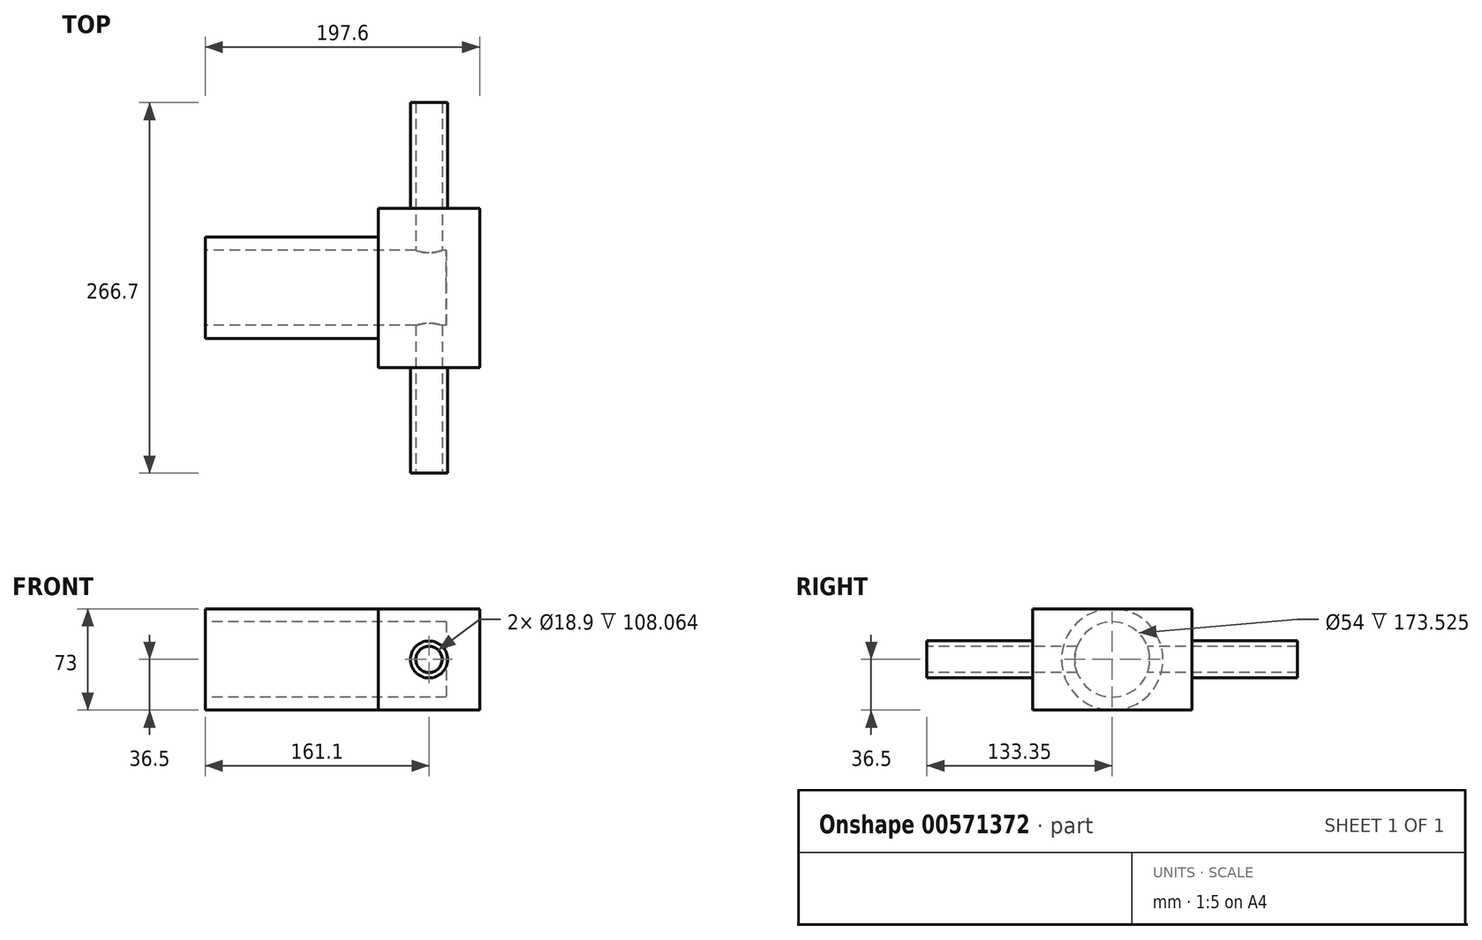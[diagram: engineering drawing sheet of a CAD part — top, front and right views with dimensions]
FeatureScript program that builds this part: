
annotation { "Feature Type Name" : "Feature", "Feature Type Description" : "" }
export const myFeature = defineFeature(function(context is Context, id is Id, definition is map)
    precondition{}
    {
        {
            var Q0;
            Q0=qCreatedBy(makeId("Front.planeOp"),FACE);
            var sketch = newSketch(context, id + "F0", { "sketchPlane" : qUnion([Q0])});
            skLineSegment(sketch, "E0.bottom", {"start": v(-36.5, -36.5) * mm, "end": v(36.5, -36.5) * mm});
            skLineSegment(sketch, "E0.top", {"start": v(-36.5, 36.5) * mm, "end": v(36.5, 36.5) * mm});
            skLineSegment(sketch, "E0.left", {"start": v(-36.5, -36.5) * mm, "end": v(-36.5, 36.5) * mm});
            skLineSegment(sketch, "E0.right", {"start": v(36.5, -36.5) * mm, "end": v(36.5, 36.5) * mm});
            skPoint(sketch, "E0.middle", {"position": v(0, 0) * mm});
            skSolve(sketch);
        }
        {
            var Q0;
            Q0 = qSketchRegion(id + "F0", true);
            extrude(context, id + "F1", {"entities" : qUnion([Q0]), "endBound" : BoundingType.SYMMETRIC, "depth" : 266.7 * mm, "offsetDistance" : 25 * mm});
        }
        {
            var Q0;
            Q0=qCreatedBy(makeId("Right.planeOp"),FACE);
            var sketch = newSketch(context, id + "F2", { "sketchPlane" : qUnion([Q0])});
            skCircle(sketch, "E1", {"center": v(0, 0) * mm, "radius": 36.5 * mm});
            skSolve(sketch);
        }
        {
            var Q0;
            Q0 = qSketchRegion(id + "F2", true);
            extrude(context, id + "F3", {"entities" : qUnion([Q0]), "operationType" : NewBodyOperationType.ADD, "oppositeDirection" : true, "depth" : 161.1 * mm, "offsetDistance" : 25 * mm});
        }
        {
            var Q0;
            Q0=makeQuery(id+"F3.opExtrude","CAP_FACE",FACE,{"disambiguationData":[OSD([sQuery(id+"F2.wireOp",EDGE,"E1")])],"isStart":false});
            var sketch = newSketch(context, id + "F4", { "sketchPlane" : qUnion([Q0])});
            skCircle(sketch, "E2", {"center": v(0, 0) * mm, "radius": 27 * mm});
            skSolve(sketch);
        }
        {
            var Q0;
            Q0 = qSketchRegion(id + "F4", true);
            extrude(context, id + "F5", {"entities" : qUnion([Q0]), "operationType" : NewBodyOperationType.REMOVE, "oppositeDirection" : true, "depth" : (12.43 + 161.1) * mm, "offsetDistance" : 25 * mm});
        }
        {
            var Q0;
            Q0=makeQuery(id+"F1.opExtrude","CAP_FACE",FACE,{"disambiguationData":[OSD([sQuery(id+"F0.wireOp",EDGE,"E0.bottom"),sQuery(id+"F0.wireOp",EDGE,"E0.top"),sQuery(id+"F0.wireOp",EDGE,"E0.left"),sQuery(id+"F0.wireOp",EDGE,"E0.right")])],"isStart":false});
            var sketch = newSketch(context, id + "F6", { "sketchPlane" : qUnion([Q0])});
            skCircle(sketch, "E3", {"center": v(0, 0) * mm, "radius": 9.45 * mm});
            skSolve(sketch);
        }
        {
            var Q0;
            Q0 = qSketchRegion(id + "F6", true);
            extrude(context, id + "F7", {"entities" : qUnion([Q0]), "operationType" : NewBodyOperationType.REMOVE, "oppositeDirection" : true, "depth" : 336 * mm, "offsetDistance" : 25 * mm});
        }
        {
            var Q0;
            Q0=makeQuery(id+"F1.opExtrude","CAP_FACE",FACE,{"disambiguationData":[OSD([sQuery(id+"F0.wireOp",EDGE,"E0.bottom"),sQuery(id+"F0.wireOp",EDGE,"E0.top"),sQuery(id+"F0.wireOp",EDGE,"E0.left"),sQuery(id+"F0.wireOp",EDGE,"E0.right")])],"isStart":true});
            var sketch = newSketch(context, id + "F8", { "sketchPlane" : qUnion([Q0])});
            skCircle(sketch, "E4", {"center": v(0, 0) * mm, "radius": 13.34 * mm});
            skCircle(sketch, "E5", {"center": v(0, 0) * mm, "radius": 57.11 * mm});
            skSolve(sketch);
        }
        {
            var Q0;
            Q0 = qSketchRegion(id + "F8", true);
            extrude(context, id + "F9", {"entities" : qUnion([Q0]), "operationType" : NewBodyOperationType.REMOVE, "oppositeDirection" : true, "depth" : 76 * mm, "offsetDistance" : 25 * mm});
        }
        {
            var Q0;
            Q0=makeQuery(id+"F1.opExtrude","CAP_FACE",FACE,{"disambiguationData":[OSD([sQuery(id+"F0.wireOp",EDGE,"E0.bottom"),sQuery(id+"F0.wireOp",EDGE,"E0.top"),sQuery(id+"F0.wireOp",EDGE,"E0.left"),sQuery(id+"F0.wireOp",EDGE,"E0.right")])],"isStart":false});
            var sketch = newSketch(context, id + "F10", { "sketchPlane" : qUnion([Q0])});
            skCircle(sketch, "E6", {"center": v(0, 0) * mm, "radius": 13.34 * mm});
            skCircle(sketch, "E7", {"center": v(0, 0) * mm, "radius": 82.5 * mm});
            skSolve(sketch);
        }
        {
            var Q0;
            Q0 = qSketchRegion(id + "F10", true);
            extrude(context, id + "F11", {"entities" : qUnion([Q0]), "operationType" : NewBodyOperationType.REMOVE, "oppositeDirection" : true, "depth" : 76 * mm, "offsetDistance" : 25 * mm});
        }
    });
